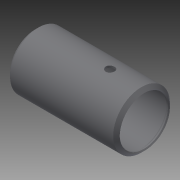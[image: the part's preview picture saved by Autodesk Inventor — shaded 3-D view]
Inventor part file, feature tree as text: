
AUTODESK INVENTOR PART (.ipt)
format: ipt  version: 2014 (Build 180170000, 170)  size: 144,896 bytes
history: native  units: in
note: dims shown in document units (in); Inventor stores cm internally (conversion verified against a paired STEP export)
features: other x56, revolve x2, sketch x2
ambient origin geometry x8: Origin, YZ Plane, XZ Plane, XY Plane, X Axis, Y Axis, Z Axis, Center Point
bodies: Solid1 (feature_tree)
feature tree (60):
  revolve  "Revolution1"  Angle=360.0deg
  revolve  "Revolution2"  [1 undecoded]
  other  "o1_XY"
  other  "o1_YZ"
  other  "o1_ZX"
  other  "o1_X"
  other  "o1_Y"
  other  "o1_Z"
  other  "o1_Center"
  other  "o2_XY"
  other  "o2_YZ"
  other  "o2_ZX"
  other  "o2_X"
  other  "o2_Y"
  other  "o2_Z"
  other  "o2_Center"
  other  "t1_XY"
  other  "t1_YZ"
  other  "t1_ZX"
  other  "t1_X"
  other  "t1_Y"
  other  "t1_Z"
  other  "t1_Center"
  other  "t2_XY"
  other  "t2_YZ"
  other  "t2_ZX"
  other  "t2_X"
  other  "t2_Y"
  other  "t2_Z"
  other  "t2_Center"
  other  "t3_XY"
  other  "t3_YZ"
  other  "t3_ZX"
  other  "t3_X"
  other  "t3_Y"
  other  "t3_Z"
  other  "t3_Center"
  other  "t4_XY"
  other  "t4_YZ"
  other  "t4_ZX"
  other  "t4_X"
  other  "t4_Y"
  other  "t4_Z"
  other  "t4_Center"
  other  "tube1_XY"
  other  "tube1_YZ"
  other  "tube1_ZX"
  other  "tube1_X"
  other  "tube1_Y"
  other  "tube1_Z"
  other  "tube1_Center"
  other  "tube2_XY"
  other  "tube2_YZ"
  other  "tube2_ZX"
  other  "tube2_X"
  other  "tube2_Y"
  other  "tube2_Z"
  other  "tube2_Center"
  sketch  "Sketch_5"
  sketch  "Sketch_1"  dims[d0=360.0deg d1=360.0deg]
note: 1 required parameter value undecoded (feature->parameter linkage not recoverable at this tier; creation-order binding heuristic only, values carry confidence <= 0.55)
